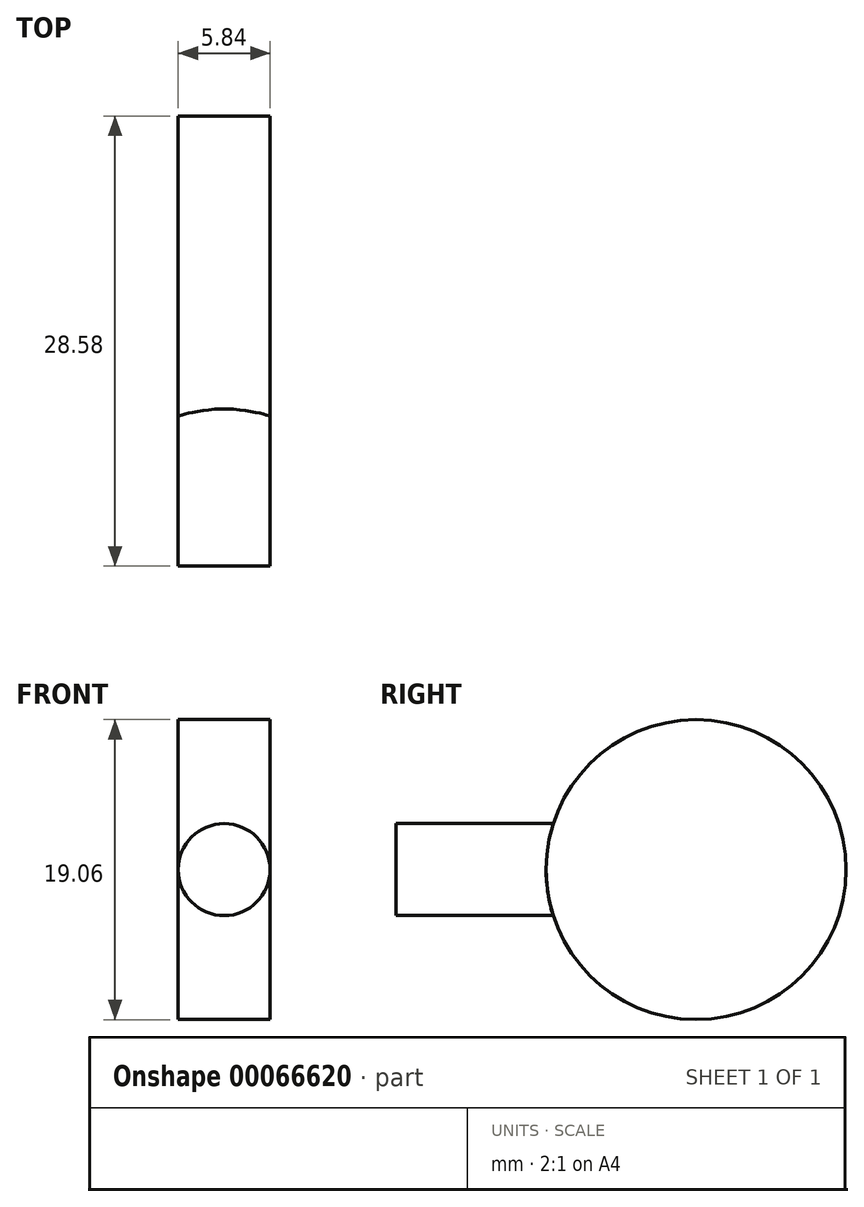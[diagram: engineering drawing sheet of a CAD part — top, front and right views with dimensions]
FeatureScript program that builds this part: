
annotation { "Feature Type Name" : "Feature", "Feature Type Description" : "" }
export const myFeature = defineFeature(function(context is Context, id is Id, definition is map)
    precondition{}
    {
        {
            var Q0;
            Q0=qCreatedBy(makeId("Front.planeOp"),FACE);
            var sketch = newSketch(context, id + "F0", { "sketchPlane" : qUnion([Q0])});
            skCircle(sketch, "E0", {"center": v(0, 0) * mm, "radius": 2.92 * mm});
            skSolve(sketch);
        }
        {
            var Q0;
            Q0=qSketchRegion(id+"F0",true);
            extrude(context, id + "F1", {"entities" : qUnion([Q0]), "depth" : 19.05 * mm});
        }
        {
            var Q0;
            Q0=qCreatedBy(makeId("Right.planeOp"),FACE);
            var sketch = newSketch(context, id + "F2", { "sketchPlane" : qUnion([Q0])});
            skCircle(sketch, "E1", {"center": v(0, 0) * mm, "radius": 9.53 * mm});
            skSolve(sketch);
        }
        {
            var Q0;
            Q0=qSketchRegion(id+"F2",true);
            extrude(context, id + "F3", {"entities" : qUnion([Q0]), "operationType" : NewBodyOperationType.ADD, "endBound" : BoundingType.SYMMETRIC, "depth" : 5.84 * mm});
        }
    });
